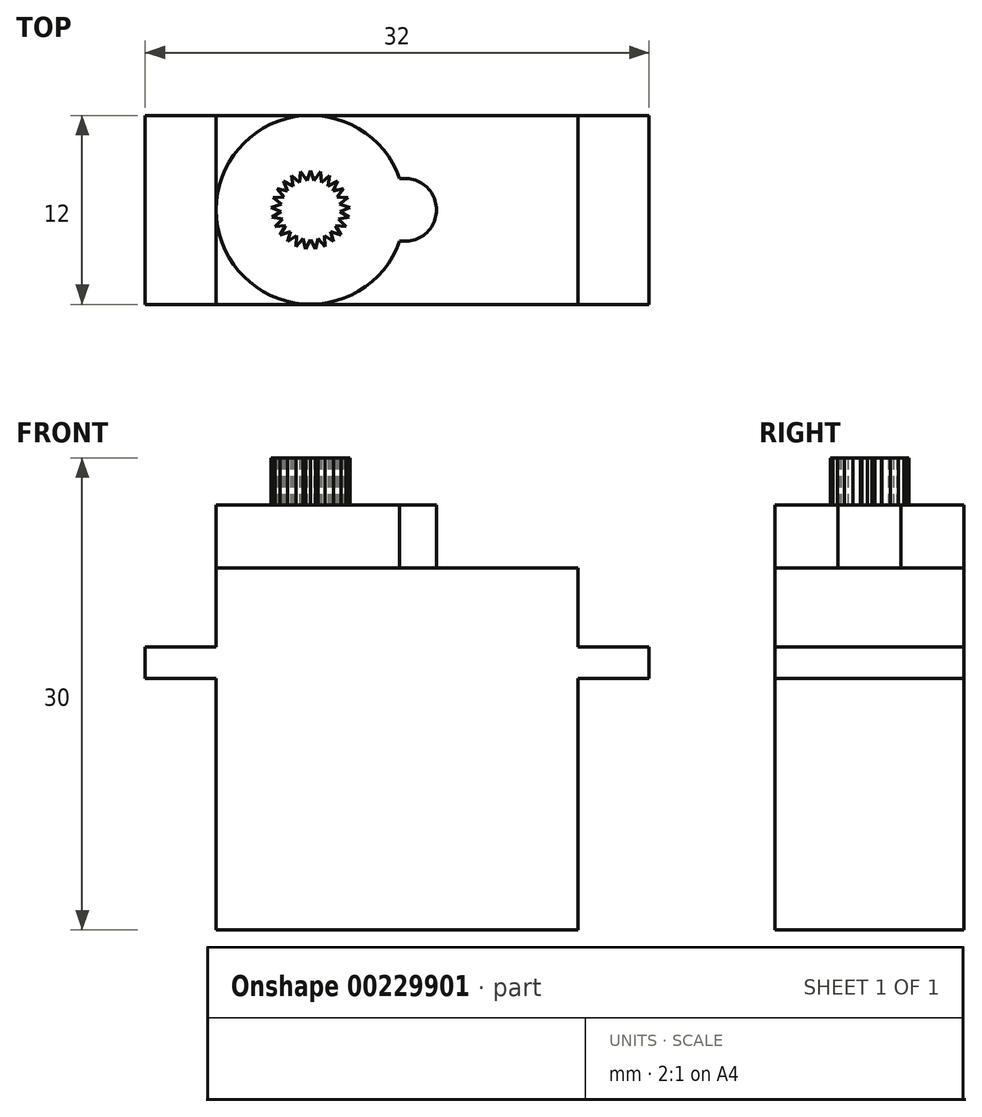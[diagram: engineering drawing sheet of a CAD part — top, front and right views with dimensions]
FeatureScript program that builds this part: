
annotation { "Feature Type Name" : "Feature", "Feature Type Description" : "" }
export const myFeature = defineFeature(function(context is Context, id is Id, definition is map)
    precondition{}
    {
        {
            var Q0;
            Q0=qCreatedBy(makeId("Front.planeOp"),FACE);
            var sketch = newSketch(context, id + "F0", { "sketchPlane" : qUnion([Q0])});
            skLineSegment(sketch, "E0.bottom", {"start": v(0, 0) * mm, "end": v(-23, 0) * mm});
            skLineSegment(sketch, "E0.top", {"start": v(0, 23) * mm, "end": v(-23, 23) * mm});
            skLineSegment(sketch, "E0.left", {"start": v(0, 0) * mm, "end": v(0, 23) * mm});
            skLineSegment(sketch, "E0.right", {"start": v(-23, 0) * mm, "end": v(-23, 23) * mm});
            skLineSegment(sketch, "E1.bottom", {"start": v(-27.5, 16) * mm, "end": v(4.5, 16) * mm});
            skLineSegment(sketch, "E1.top", {"start": v(-27.5, 18) * mm, "end": v(4.5, 18) * mm});
            skLineSegment(sketch, "E1.left", {"start": v(-27.5, 16) * mm, "end": v(-27.5, 18) * mm});
            skLineSegment(sketch, "E1.right", {"start": v(4.5, 16) * mm, "end": v(4.5, 18) * mm});
            skLineSegment(sketch, "E2.bottom", {"start": v(-23, 23) * mm, "end": v(-17, 23) * mm});
            skLineSegment(sketch, "E2.top", {"start": v(-23, 27) * mm, "end": v(-17, 27) * mm});
            skLineSegment(sketch, "E2.left", {"start": v(-23, 23) * mm, "end": v(-23, 27) * mm});
            skLineSegment(sketch, "E2.right", {"start": v(-17, 23) * mm, "end": v(-17, 27) * mm});
            skLineSegment(sketch, "E3", {"start": v(-11, 27) * mm, "end": v(-9, 27) * mm});
            skLineSegment(sketch, "E4", {"start": v(-9, 27) * mm, "end": v(-9, 23) * mm});
            skLineSegment(sketch, "E5", {"start": v(-11, 27) * mm, "end": v(-11, 23) * mm});
            skLineSegment(sketch, "E6", {"start": v(-11, 23) * mm, "end": v(-9, 23) * mm});
            skPoint(sketch, "E7", {"position": v(-11.5, 16) * mm});
            skSolve(sketch);
        }
        {
            var Q0;
            Q0=makeQuery(id+"F0.imprint","IMPRINT",FACE,{"disambiguationData":[TD([[makeQuery(id+"F0.imprint","IMPRINT",EDGE,{"derivedFrom":sQuery(id+"F0.wireOp",EDGE,"E2.top")}),-1.0]])]});
            var Q1;
            Q1=sQuery(id+"F0.wireOp",EDGE,"E2.right");
            revolve(context, id + "F1", {"entities" : qUnion([Q0]), "axis" : qUnion([Q1]), "revolveType" : RevolveType.FULL});
        }
        {
            var Q0;
            Q0=makeQuery(id+"F0.imprint","IMPRINT",FACE,{"disambiguationData":[TD([[makeQuery(id+"F0.imprint","IMPRINT",EDGE,{"derivedFrom":sQuery(id+"F0.wireOp",EDGE,"E3")}),-1.0]])]});
            var Q1;
            Q1=sQuery(id+"F0.wireOp",EDGE,"E5");
            revolve(context, id + "F2", {"operationType" : NewBodyOperationType.ADD, "entities" : qUnion([Q0]), "axis" : qUnion([Q1]), "revolveType" : RevolveType.FULL});
        }
        {
            var Q0;
            {var subQ0=sQuery(id+"F0.wireOp",EDGE,"E0.bottom");Q0=makeQuery(id+"F0.imprint","IMPRINT",FACE,{"disambiguationData":[TD([[makeQuery(id+"F0.imprint","IMPRINT",EDGE,{"derivedFrom":subQ0}),-1.0]])]});}
            var Q1;
            {var subQ0=sQuery(id+"F0.wireOp",EDGE,"E1.top");var subQ1=sQuery(id+"F0.wireOp",EDGE,"E0.left");var subQ2=makeQuery(id+"F0.imprint","INTERSECT",VERTEX,{"derivedFrom":[subQ1,subQ0]});Q1=makeQuery(id+"F0.imprint","IMPRINT",FACE,{"disambiguationData":[TD([[makeQuery(id+"F0.imprint","IMPRINT",EDGE,{"disambiguationData":[TD([[subQ2,1.0]])],"derivedFrom":subQ1}),1.0]])]});}
            var Q2;
            {var subQ5=sQuery(id+"F0.wireOp",EDGE,"E1.right");Q2=makeQuery(id+"F0.imprint","IMPRINT",FACE,{"disambiguationData":[TD([[makeQuery(id+"F0.imprint","IMPRINT",EDGE,{"derivedFrom":subQ5}),1.0]])]});}
            var Q3;
            {var subQ5=sQuery(id+"F0.wireOp",EDGE,"E1.left");Q3=makeQuery(id+"F0.imprint","IMPRINT",FACE,{"disambiguationData":[TD([[makeQuery(id+"F0.imprint","IMPRINT",EDGE,{"derivedFrom":subQ5}),-1.0]])]});}
            var Q4;
            {var subQ0=sQuery(id+"F0.wireOp",EDGE,"E0.top");var subQ5=sQuery(id+"F0.wireOp",EDGE,"E0.left");var subQ10=makeQuery(id+"F0.imprint","INTERSECT",VERTEX,{"derivedFrom":[subQ0,subQ5]});Q4=makeQuery(id+"F0.imprint","IMPRINT",FACE,{"disambiguationData":[TD([[makeQuery(id+"F0.imprint","IMPRINT",EDGE,{"disambiguationData":[TD([[subQ10,-1.0]])],"derivedFrom":subQ0}),1.0]])]});}
            extrude(context, id + "F3", {"entities" : qUnion([Q0, Q1, Q2, Q3, Q4]), "operationType" : NewBodyOperationType.ADD, "depth" : 12 * mm, "symmetric" : true});
        }
        {
            var Q0;
            Q0=qCreatedBy(makeId("Top.planeOp"),FACE);
            var sketch = newSketch(context, id + "F4", { "sketchPlane" : qUnion([Q0])});
            skCircle(sketch, "E8", {"center": v(-17, 0) * mm, "radius": 2.5 * mm});
            skCircle(sketch, "E9", {"center": v(-17, 0) * mm, "radius": 1.88 * mm, "construction": true});
            skLineSegment(sketch, "E10", {"start": v(-17, 2.5) * mm, "end": v(-17.23, 1.86) * mm});
            skLineSegment(sketch, "E11", {"start": v(-17.62, 2.42) * mm, "end": v(-17.23, 1.86) * mm});
            skLineSegment(sketch, "E12", {"start": v(-17.62, 2.42) * mm, "end": v(-17.7, 1.74) * mm});
            skLineSegment(sketch, "E13", {"start": v(-17.7, 1.74) * mm, "end": v(-18.2, 2.2) * mm});
            skLineSegment(sketch, "E14", {"start": v(-18.2, 2.2) * mm, "end": v(-18.1, 1.52) * mm});
            skLineSegment(sketch, "E15", {"start": v(-18.1, 1.52) * mm, "end": v(-18.71, 1.82) * mm});
            skLineSegment(sketch, "E16", {"start": v(-18.71, 1.82) * mm, "end": v(-18.44, 1.2) * mm});
            skLineSegment(sketch, "E17", {"start": v(-18.44, 1.2) * mm, "end": v(-19.11, 1.34) * mm});
            skLineSegment(sketch, "E18", {"start": v(-17, 2.5) * mm, "end": v(-16.77, 1.86) * mm});
            skLineSegment(sketch, "E19", {"start": v(-16.77, 1.86) * mm, "end": v(-16.38, 2.42) * mm});
            skLineSegment(sketch, "E20", {"start": v(-16.38, 2.42) * mm, "end": v(-16.3, 1.74) * mm});
            skLineSegment(sketch, "E21", {"start": v(-16.3, 1.74) * mm, "end": v(-15.8, 2.2) * mm});
            skLineSegment(sketch, "E22", {"start": v(-15.8, 2.2) * mm, "end": v(-15.9, 1.52) * mm});
            skLineSegment(sketch, "E23", {"start": v(-15.9, 1.52) * mm, "end": v(-15.29, 1.82) * mm});
            skLineSegment(sketch, "E24", {"start": v(-15.29, 1.82) * mm, "end": v(-15.56, 1.2) * mm});
            skLineSegment(sketch, "E25", {"start": v(-15.56, 1.2) * mm, "end": v(-14.89, 1.34) * mm});
            skLineSegment(sketch, "E26", {"start": v(-14.89, 1.34) * mm, "end": v(-15.3, 0.8) * mm});
            skLineSegment(sketch, "E27", {"start": v(-15.3, 0.8) * mm, "end": v(-14.62, 0.77) * mm});
            skLineSegment(sketch, "E28", {"start": v(-14.62, 0.77) * mm, "end": v(-15.16, 0.35) * mm});
            skLineSegment(sketch, "E29", {"start": v(-15.16, 0.35) * mm, "end": v(-14.5, 0.16) * mm});
            skLineSegment(sketch, "E30", {"start": v(-14.5, 0.16) * mm, "end": v(-15.13, -0.12) * mm});
            skLineSegment(sketch, "E31", {"start": v(-15.13, -0.12) * mm, "end": v(-14.54, -0.47) * mm});
            skLineSegment(sketch, "E32", {"start": v(-15.22, -0.58) * mm, "end": v(-14.54, -0.47) * mm});
            skLineSegment(sketch, "E33", {"start": v(-15.22, -0.58) * mm, "end": v(-14.74, -1.06) * mm});
            skLineSegment(sketch, "E34", {"start": v(-14.74, -1.06) * mm, "end": v(-15.42, -1) * mm});
            skLineSegment(sketch, "E35", {"start": v(-15.42, -1) * mm, "end": v(-15.07, -1.6) * mm});
            skLineSegment(sketch, "E36", {"start": v(-15.07, -1.6) * mm, "end": v(-15.72, -1.37) * mm});
            skLineSegment(sketch, "E37", {"start": v(-15.72, -1.37) * mm, "end": v(-15.53, -2.02) * mm});
            skLineSegment(sketch, "E38", {"start": v(-15.53, -2.02) * mm, "end": v(-16.1, -1.64) * mm});
            skLineSegment(sketch, "E39", {"start": v(-16.1, -1.64) * mm, "end": v(-16.08, -2.32) * mm});
            skLineSegment(sketch, "E40", {"start": v(-16.08, -2.32) * mm, "end": v(-16.53, -1.82) * mm});
            skLineSegment(sketch, "E41", {"start": v(-17, -1.87) * mm, "end": v(-17.31, -2.48) * mm});
            skLineSegment(sketch, "E42", {"start": v(-16.53, -1.82) * mm, "end": v(-16.69, -2.48) * mm});
            skLineSegment(sketch, "E43", {"start": v(-16.69, -2.48) * mm, "end": v(-17, -1.87) * mm});
            skLineSegment(sketch, "E44", {"start": v(-17.31, -2.48) * mm, "end": v(-17.47, -1.82) * mm});
            skLineSegment(sketch, "E45", {"start": v(-17.47, -1.82) * mm, "end": v(-17.92, -2.32) * mm});
            skLineSegment(sketch, "E46", {"start": v(-17.92, -2.32) * mm, "end": v(-17.9, -1.64) * mm});
            skLineSegment(sketch, "E47", {"start": v(-17.9, -1.64) * mm, "end": v(-18.47, -2.02) * mm});
            skLineSegment(sketch, "E48", {"start": v(-18.47, -2.02) * mm, "end": v(-18.28, -1.37) * mm});
            skLineSegment(sketch, "E49", {"start": v(-18.28, -1.37) * mm, "end": v(-18.93, -1.6) * mm});
            skLineSegment(sketch, "E50", {"start": v(-18.93, -1.6) * mm, "end": v(-18.58, -1) * mm});
            skLineSegment(sketch, "E51", {"start": v(-18.58, -1) * mm, "end": v(-19.26, -1.06) * mm});
            skLineSegment(sketch, "E52", {"start": v(-19.26, -1.06) * mm, "end": v(-18.78, -0.58) * mm});
            skLineSegment(sketch, "E53", {"start": v(-18.78, -0.58) * mm, "end": v(-19.46, -0.47) * mm});
            skLineSegment(sketch, "E54", {"start": v(-19.46, -0.47) * mm, "end": v(-18.87, -0.12) * mm});
            skLineSegment(sketch, "E55", {"start": v(-18.87, -0.12) * mm, "end": v(-19.5, 0.16) * mm});
            skLineSegment(sketch, "E56", {"start": v(-19.5, 0.16) * mm, "end": v(-18.84, 0.35) * mm});
            skLineSegment(sketch, "E57", {"start": v(-18.84, 0.35) * mm, "end": v(-19.38, 0.77) * mm});
            skLineSegment(sketch, "E58", {"start": v(-19.38, 0.77) * mm, "end": v(-18.7, 0.8) * mm});
            skLineSegment(sketch, "E59", {"start": v(-18.7, 0.8) * mm, "end": v(-19.11, 1.34) * mm});
            skCircle(sketch, "E60", {"center": v(-17, 0) * mm, "radius": 4 * mm});
            skLineSegment(sketch, "E61.0", {"start": v(-17, -1.88) * mm, "end": v(-17.47, -1.82) * mm});
            skLineSegment(sketch, "E61.1", {"start": v(-17.47, -1.82) * mm, "end": v(-17.9, -1.64) * mm});
            skLineSegment(sketch, "E61.2", {"start": v(-17.9, -1.64) * mm, "end": v(-18.28, -1.37) * mm});
            skLineSegment(sketch, "E61.3", {"start": v(-18.28, -1.37) * mm, "end": v(-18.58, -1) * mm});
            skLineSegment(sketch, "E61.4", {"start": v(-18.58, -1) * mm, "end": v(-18.78, -0.58) * mm});
            skLineSegment(sketch, "E61.5", {"start": v(-18.78, -0.58) * mm, "end": v(-18.87, -0.12) * mm});
            skLineSegment(sketch, "E61.6", {"start": v(-18.87, -0.12) * mm, "end": v(-18.84, 0.35) * mm});
            skLineSegment(sketch, "E61.7", {"start": v(-18.84, 0.35) * mm, "end": v(-18.7, 0.8) * mm});
            skLineSegment(sketch, "E61.8", {"start": v(-18.7, 0.8) * mm, "end": v(-18.44, 1.2) * mm});
            skLineSegment(sketch, "E61.9", {"start": v(-18.44, 1.2) * mm, "end": v(-18.1, 1.52) * mm});
            skLineSegment(sketch, "E61.10", {"start": v(-18.1, 1.52) * mm, "end": v(-17.7, 1.74) * mm});
            skLineSegment(sketch, "E61.11", {"start": v(-17.7, 1.74) * mm, "end": v(-17.23, 1.86) * mm});
            skLineSegment(sketch, "E61.12", {"start": v(-17.23, 1.86) * mm, "end": v(-16.77, 1.86) * mm});
            skLineSegment(sketch, "E61.13", {"start": v(-16.77, 1.86) * mm, "end": v(-16.3, 1.74) * mm});
            skLineSegment(sketch, "E61.14", {"start": v(-16.3, 1.74) * mm, "end": v(-15.9, 1.52) * mm});
            skLineSegment(sketch, "E61.15", {"start": v(-15.9, 1.52) * mm, "end": v(-15.56, 1.2) * mm});
            skLineSegment(sketch, "E61.16", {"start": v(-15.56, 1.2) * mm, "end": v(-15.3, 0.8) * mm});
            skLineSegment(sketch, "E61.17", {"start": v(-15.3, 0.8) * mm, "end": v(-15.16, 0.35) * mm});
            skLineSegment(sketch, "E61.18", {"start": v(-15.16, 0.35) * mm, "end": v(-15.13, -0.12) * mm});
            skLineSegment(sketch, "E61.19", {"start": v(-15.13, -0.12) * mm, "end": v(-15.22, -0.58) * mm});
            skLineSegment(sketch, "E61.20", {"start": v(-15.22, -0.58) * mm, "end": v(-15.42, -1) * mm});
            skLineSegment(sketch, "E61.21", {"start": v(-15.42, -1) * mm, "end": v(-15.72, -1.37) * mm});
            skLineSegment(sketch, "E61.22", {"start": v(-15.72, -1.37) * mm, "end": v(-16.1, -1.64) * mm});
            skLineSegment(sketch, "E61.23", {"start": v(-16.1, -1.64) * mm, "end": v(-16.53, -1.82) * mm});
            skLineSegment(sketch, "E61.24", {"start": v(-16.53, -1.82) * mm, "end": v(-17, -1.87) * mm});
            skPoint(sketch, "E62", {"position": v(-13, 0) * mm});
            skSolve(sketch);
        }
        {
            var Q0;
            Q0=makeQuery(id+"F4.imprint","IMPRINT",FACE,{"disambiguationData":[TD([[makeQuery(id+"F4.imprint","IMPRINT",EDGE,{"derivedFrom":sQuery(id+"F4.wireOp",EDGE,"E61.0")}),-1.0]])]});
            var Q1;
            Q1=makeQuery(id+"F4.imprint","IMPRINT",FACE,{"disambiguationData":[TD([[makeQuery(id+"F4.imprint","IMPRINT",EDGE,{"derivedFrom":sQuery(id+"F4.wireOp",EDGE,"E17")}),1.0]])]});
            var Q2;
            Q2=makeQuery(id+"F4.imprint","IMPRINT",FACE,{"disambiguationData":[TD([[makeQuery(id+"F4.imprint","IMPRINT",EDGE,{"derivedFrom":sQuery(id+"F4.wireOp",EDGE,"E57")}),-1.0]])]});
            var Q3;
            Q3=makeQuery(id+"F4.imprint","IMPRINT",FACE,{"disambiguationData":[TD([[makeQuery(id+"F4.imprint","IMPRINT",EDGE,{"derivedFrom":sQuery(id+"F4.wireOp",EDGE,"E55")}),-1.0]])]});
            var Q4;
            Q4=makeQuery(id+"F4.imprint","IMPRINT",FACE,{"disambiguationData":[TD([[makeQuery(id+"F4.imprint","IMPRINT",EDGE,{"derivedFrom":sQuery(id+"F4.wireOp",EDGE,"E53")}),-1.0]])]});
            var Q5;
            Q5=makeQuery(id+"F4.imprint","IMPRINT",FACE,{"disambiguationData":[TD([[makeQuery(id+"F4.imprint","IMPRINT",EDGE,{"derivedFrom":sQuery(id+"F4.wireOp",EDGE,"E51")}),-1.0]])]});
            var Q6;
            Q6=makeQuery(id+"F4.imprint","IMPRINT",FACE,{"disambiguationData":[TD([[makeQuery(id+"F4.imprint","IMPRINT",EDGE,{"derivedFrom":sQuery(id+"F4.wireOp",EDGE,"E49")}),-1.0]])]});
            var Q7;
            Q7=makeQuery(id+"F4.imprint","IMPRINT",FACE,{"disambiguationData":[TD([[makeQuery(id+"F4.imprint","IMPRINT",EDGE,{"derivedFrom":sQuery(id+"F4.wireOp",EDGE,"E47")}),-1.0]])]});
            var Q8;
            Q8=makeQuery(id+"F4.imprint","IMPRINT",FACE,{"disambiguationData":[TD([[makeQuery(id+"F4.imprint","IMPRINT",EDGE,{"derivedFrom":sQuery(id+"F4.wireOp",EDGE,"E45")}),-1.0]])]});
            var Q9;
            Q9=makeQuery(id+"F4.imprint","IMPRINT",FACE,{"disambiguationData":[TD([[makeQuery(id+"F4.imprint","IMPRINT",EDGE,{"derivedFrom":sQuery(id+"F4.wireOp",EDGE,"E41")}),-1.0]])]});
            var Q10;
            Q10=makeQuery(id+"F4.imprint","IMPRINT",FACE,{"disambiguationData":[TD([[makeQuery(id+"F4.imprint","IMPRINT",EDGE,{"derivedFrom":sQuery(id+"F4.wireOp",EDGE,"E42")}),-1.0]])]});
            var Q11;
            Q11=makeQuery(id+"F4.imprint","IMPRINT",FACE,{"disambiguationData":[TD([[makeQuery(id+"F4.imprint","IMPRINT",EDGE,{"derivedFrom":sQuery(id+"F4.wireOp",EDGE,"E39")}),-1.0]])]});
            var Q12;
            Q12=makeQuery(id+"F4.imprint","IMPRINT",FACE,{"disambiguationData":[TD([[makeQuery(id+"F4.imprint","IMPRINT",EDGE,{"derivedFrom":sQuery(id+"F4.wireOp",EDGE,"E37")}),-1.0]])]});
            var Q13;
            Q13=makeQuery(id+"F4.imprint","IMPRINT",FACE,{"disambiguationData":[TD([[makeQuery(id+"F4.imprint","IMPRINT",EDGE,{"derivedFrom":sQuery(id+"F4.wireOp",EDGE,"E35")}),-1.0]])]});
            var Q14;
            Q14=makeQuery(id+"F4.imprint","IMPRINT",FACE,{"disambiguationData":[TD([[makeQuery(id+"F4.imprint","IMPRINT",EDGE,{"derivedFrom":sQuery(id+"F4.wireOp",EDGE,"E33")}),-1.0]])]});
            var Q15;
            Q15=makeQuery(id+"F4.imprint","IMPRINT",FACE,{"disambiguationData":[TD([[makeQuery(id+"F4.imprint","IMPRINT",EDGE,{"derivedFrom":sQuery(id+"F4.wireOp",EDGE,"E31")}),-1.0]])]});
            var Q16;
            Q16=makeQuery(id+"F4.imprint","IMPRINT",FACE,{"disambiguationData":[TD([[makeQuery(id+"F4.imprint","IMPRINT",EDGE,{"derivedFrom":sQuery(id+"F4.wireOp",EDGE,"E29")}),-1.0]])]});
            var Q17;
            Q17=makeQuery(id+"F4.imprint","IMPRINT",FACE,{"disambiguationData":[TD([[makeQuery(id+"F4.imprint","IMPRINT",EDGE,{"derivedFrom":sQuery(id+"F4.wireOp",EDGE,"E23")}),-1.0]])]});
            var Q18;
            Q18=makeQuery(id+"F4.imprint","IMPRINT",FACE,{"disambiguationData":[TD([[makeQuery(id+"F4.imprint","IMPRINT",EDGE,{"derivedFrom":sQuery(id+"F4.wireOp",EDGE,"E25")}),-1.0]])]});
            var Q19;
            Q19=makeQuery(id+"F4.imprint","IMPRINT",FACE,{"disambiguationData":[TD([[makeQuery(id+"F4.imprint","IMPRINT",EDGE,{"derivedFrom":sQuery(id+"F4.wireOp",EDGE,"E27")}),-1.0]])]});
            var Q20;
            Q20=makeQuery(id+"F4.imprint","IMPRINT",FACE,{"disambiguationData":[TD([[makeQuery(id+"F4.imprint","IMPRINT",EDGE,{"derivedFrom":sQuery(id+"F4.wireOp",EDGE,"E15")}),1.0]])]});
            var Q21;
            Q21=makeQuery(id+"F4.imprint","IMPRINT",FACE,{"disambiguationData":[TD([[makeQuery(id+"F4.imprint","IMPRINT",EDGE,{"derivedFrom":sQuery(id+"F4.wireOp",EDGE,"E13")}),1.0]])]});
            var Q22;
            Q22=makeQuery(id+"F4.imprint","IMPRINT",FACE,{"disambiguationData":[TD([[makeQuery(id+"F4.imprint","IMPRINT",EDGE,{"derivedFrom":sQuery(id+"F4.wireOp",EDGE,"E11")}),-1.0]])]});
            var Q23;
            Q23=makeQuery(id+"F4.imprint","IMPRINT",FACE,{"disambiguationData":[TD([[makeQuery(id+"F4.imprint","IMPRINT",EDGE,{"derivedFrom":sQuery(id+"F4.wireOp",EDGE,"E10")}),1.0]])]});
            var Q24;
            Q24=makeQuery(id+"F4.imprint","IMPRINT",FACE,{"disambiguationData":[TD([[makeQuery(id+"F4.imprint","IMPRINT",EDGE,{"derivedFrom":sQuery(id+"F4.wireOp",EDGE,"E19")}),-1.0]])]});
            var Q25;
            Q25=makeQuery(id+"F4.imprint","IMPRINT",FACE,{"disambiguationData":[TD([[makeQuery(id+"F4.imprint","IMPRINT",EDGE,{"derivedFrom":sQuery(id+"F4.wireOp",EDGE,"E21")}),-1.0]])]});
            extrude(context, id + "F5", {"entities" : qUnion([Q0, Q1, Q2, Q3, Q4, Q5, Q6, Q7, Q8, Q9, Q10, Q11, Q12, Q13, Q14, Q15, Q16, Q17, Q18, Q19, Q20, Q21, Q22, Q23, Q24, Q25]), "depth" : 30 * mm, "hasSecondDirection" : true, "secondDirectionOppositeDirection" : false, "secondDirectionDepth" : 27 * mm});
        }
    });
